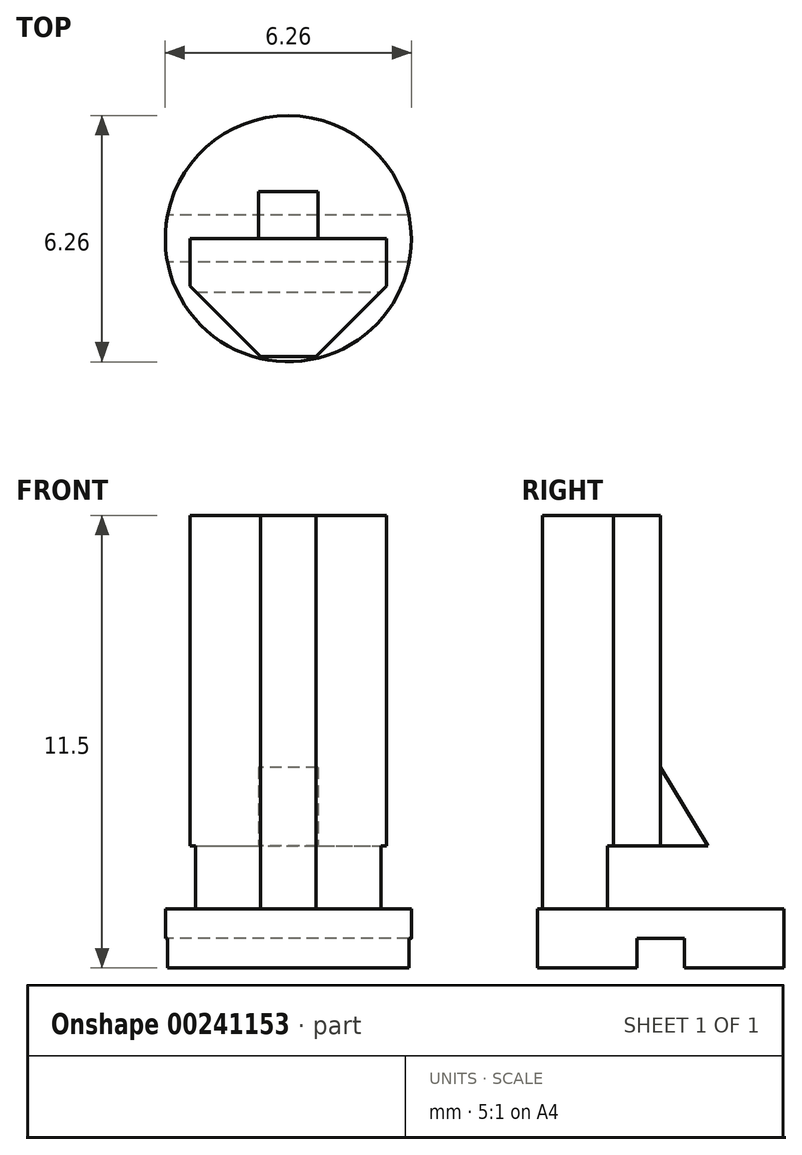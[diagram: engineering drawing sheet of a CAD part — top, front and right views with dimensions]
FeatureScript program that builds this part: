
annotation { "Feature Type Name" : "Feature", "Feature Type Description" : "" }
export const myFeature = defineFeature(function(context is Context, id is Id, definition is map)
    precondition{}
    {
        {
            var Q0;
            Q0=qCreatedBy(makeId("Top.planeOp"),FACE);
            var sketch = newSketch(context, id + "F0", { "sketchPlane" : qUnion([Q0])});
            skCircle(sketch, "E0", {"center": v(0, 0) * mm, "radius": 3.12 * mm});
            skLineSegment(sketch, "E1", {"start": v(3.07, 0.6) * mm, "end": v(-3.07, 0.6) * mm});
            skLineSegment(sketch, "E2", {"start": v(3.07, -0.6) * mm, "end": v(-3.07, -0.6) * mm});
            skSolve(sketch);
        }
        {
            var Q0;
            {var subQ0=sQuery(id+"F0.wireOp",EDGE,"E1");Q0=makeQuery(id+"F0.imprint","IMPRINT",FACE,{"disambiguationData":[TD([[makeQuery(id+"F0.imprint","IMPRINT",EDGE,{"derivedFrom":subQ0}),-1.0]])]});}
            var Q1;
            {var subQ0=sQuery(id+"F0.wireOp",EDGE,"E1");Q1=makeQuery(id+"F0.imprint","IMPRINT",FACE,{"disambiguationData":[TD([[makeQuery(id+"F0.imprint","IMPRINT",EDGE,{"derivedFrom":subQ0}),1.0]])]});}
            var Q2;
            {var subQ0=sQuery(id+"F0.wireOp",EDGE,"E2");Q2=makeQuery(id+"F0.imprint","IMPRINT",FACE,{"disambiguationData":[TD([[makeQuery(id+"F0.imprint","IMPRINT",EDGE,{"derivedFrom":subQ0}),1.0]])]});}
            extrude(context, id + "F1", {"entities" : qUnion([Q0, Q1, Q2]), "depth" : 1.5 * mm});
        }
        {
            var Q0;
            {var subQ0=sQuery(id+"F0.wireOp",EDGE,"E1");Q0=makeQuery(id+"F0.imprint","IMPRINT",FACE,{"disambiguationData":[TD([[makeQuery(id+"F0.imprint","IMPRINT",EDGE,{"derivedFrom":subQ0}),1.0]])]});}
            var Q1;
            Q1=makeQuery(id+"F1.opExtrude","CAP_FACE",FACE,{"disambiguationData":[OSD([sQuery(id+"F0.wireOp",EDGE,"E0")])],"isStart":false});
            extrude(context, id + "F2", {"entities" : qUnion([Q0]), "operationType" : NewBodyOperationType.REMOVE, "endBoundEntityFace" : qUnion([Q1]), "depth" : 0.75 * mm});
        }
        {
            var Q0;
            Q0=makeQuery(id+"F1.opExtrude","CAP_FACE",FACE,{"disambiguationData":[OSD([sQuery(id+"F0.wireOp",EDGE,"E0")])],"isStart":false});
            var sketch = newSketch(context, id + "F3", { "sketchPlane" : qUnion([Q0])});
            skLineSegment(sketch, "E3.bottom", {"start": v(-2.5, 0) * mm, "end": v(2.5, 0) * mm});
            skLineSegment(sketch, "E3.top", {"start": v(-2.5, -3) * mm, "end": v(2.5, -3) * mm});
            skLineSegment(sketch, "E3.left", {"start": v(-2.5, 0) * mm, "end": v(-2.5, -3) * mm});
            skLineSegment(sketch, "E3.right", {"start": v(2.5, 0) * mm, "end": v(2.5, -3) * mm});
            skSolve(sketch);
        }
        {
            var Q0;
            {var subQ0=sQuery(id+"F3.wireOp",EDGE,"E3.left");var subQ1=sQuery(id+"F3.wireOp",EDGE,"E3.top");var subQ2=makeQuery(id+"F3.imprint","INTERSECT",VERTEX,{"derivedFrom":[subQ1,subQ0]});Q0=makeQuery(id+"F3.imprint","IMPRINT",FACE,{"disambiguationData":[TD([[makeQuery(id+"F3.imprint","IMPRINT",EDGE,{"disambiguationData":[TD([[subQ2,-1.0]])],"derivedFrom":subQ1}),1.0]])]});}
            var Q1;
            {var subQ1=sQuery(id+"F3.wireOp",EDGE,"E3.bottom");Q1=makeQuery(id+"F3.imprint","IMPRINT",FACE,{"disambiguationData":[TD([[makeQuery(id+"F3.imprint","IMPRINT",EDGE,{"derivedFrom":subQ1}),-1.0]])]});}
            var Q2;
            {var subQ0=sQuery(id+"F3.wireOp",EDGE,"E3.right");var subQ1=sQuery(id+"F3.wireOp",EDGE,"E3.top");var subQ2=makeQuery(id+"F3.imprint","INTERSECT",VERTEX,{"derivedFrom":[subQ1,subQ0]});Q2=makeQuery(id+"F3.imprint","IMPRINT",FACE,{"disambiguationData":[TD([[makeQuery(id+"F3.imprint","IMPRINT",EDGE,{"disambiguationData":[TD([[subQ2,1.0]])],"derivedFrom":subQ1}),1.0]])]});}
            extrude(context, id + "F4", {"entities" : qUnion([Q0, Q1, Q2]), "operationType" : NewBodyOperationType.ADD, "depth" : 10 * mm});
        }
        {
            var Q0;
            Q0=makeQuery(id+"F4.opExtrude","SWEPT_EDGE",EDGE,{"disambiguationData":[OSD([sQuery(id+"F3.wireOp",EDGE,"E3.top"),sQuery(id+"F3.wireOp",EDGE,"E3.left")])]});
            var Q1;
            Q1=makeQuery(id+"F4.opExtrude","SWEPT_EDGE",EDGE,{"disambiguationData":[OSD([sQuery(id+"F3.wireOp",EDGE,"E3.top"),sQuery(id+"F3.wireOp",EDGE,"E3.right")])]});
            chamfer(context, id + "F5", {"entities" : qUnion([Q0, Q1]), "width" : 1.8 * mm, "tangentPropagation" : true});
        }
        {
            var Q0;
            Q0=qCreatedBy(makeId("Right.planeOp"),FACE);
            var sketch = newSketch(context, id + "F6", { "sketchPlane" : qUnion([Q0])});
            skLineSegment(sketch, "E4.bottom", {"start": v(0, 3.1) * mm, "end": v(-1.35, 3.1) * mm});
            skLineSegment(sketch, "E4.top", {"start": v(0, 1.5) * mm, "end": v(-1.35, 1.5) * mm});
            skLineSegment(sketch, "E4.left", {"start": v(0, 3.1) * mm, "end": v(0, 1.5) * mm});
            skLineSegment(sketch, "E4.right", {"start": v(-1.35, 3.1) * mm, "end": v(-1.35, 1.5) * mm});
            skSolve(sketch);
        }
        {
            var Q0;
            Q0 = qSketchRegion(id + "F6", true);
            extrude(context, id + "F7", {"entities" : qUnion([Q0]), "operationType" : NewBodyOperationType.REMOVE, "endBound" : BoundingType.THROUGH_ALL, "oppositeDirection" : true, "depth" : 25 * mm, "hasSecondDirection" : true, "secondDirectionOppositeDirection" : false, "secondDirectionDepth" : 25 * mm});
        }
        {
            var Q0;
            Q0=qCreatedBy(makeId("Right.planeOp"),FACE);
            var sketch = newSketch(context, id + "F8", { "sketchPlane" : qUnion([Q0])});
            skLineSegment(sketch, "E5", {"start": v(0, 3.1) * mm, "end": v(1.2, 3.1) * mm});
            skLineSegment(sketch, "E6", {"start": v(1.2, 3.1) * mm, "end": v(0, 5.1) * mm});
            skLineSegment(sketch, "E7", {"start": v(0, 5.1) * mm, "end": v(0, 3.1) * mm});
            skSolve(sketch);
        }
        {
            var Q0;
            Q0=makeQuery(id+"F8.imprint","IMPRINT",FACE,{"disambiguationData":[TD([[makeQuery(id+"F8.imprint","IMPRINT",EDGE,{"derivedFrom":sQuery(id+"F8.wireOp",EDGE,"E5")}),1.0]])]});
            extrude(context, id + "F9", {"entities" : qUnion([Q0]), "operationType" : NewBodyOperationType.ADD, "endBound" : BoundingType.SYMMETRIC, "depth" : 1.5 * mm});
        }
    });
